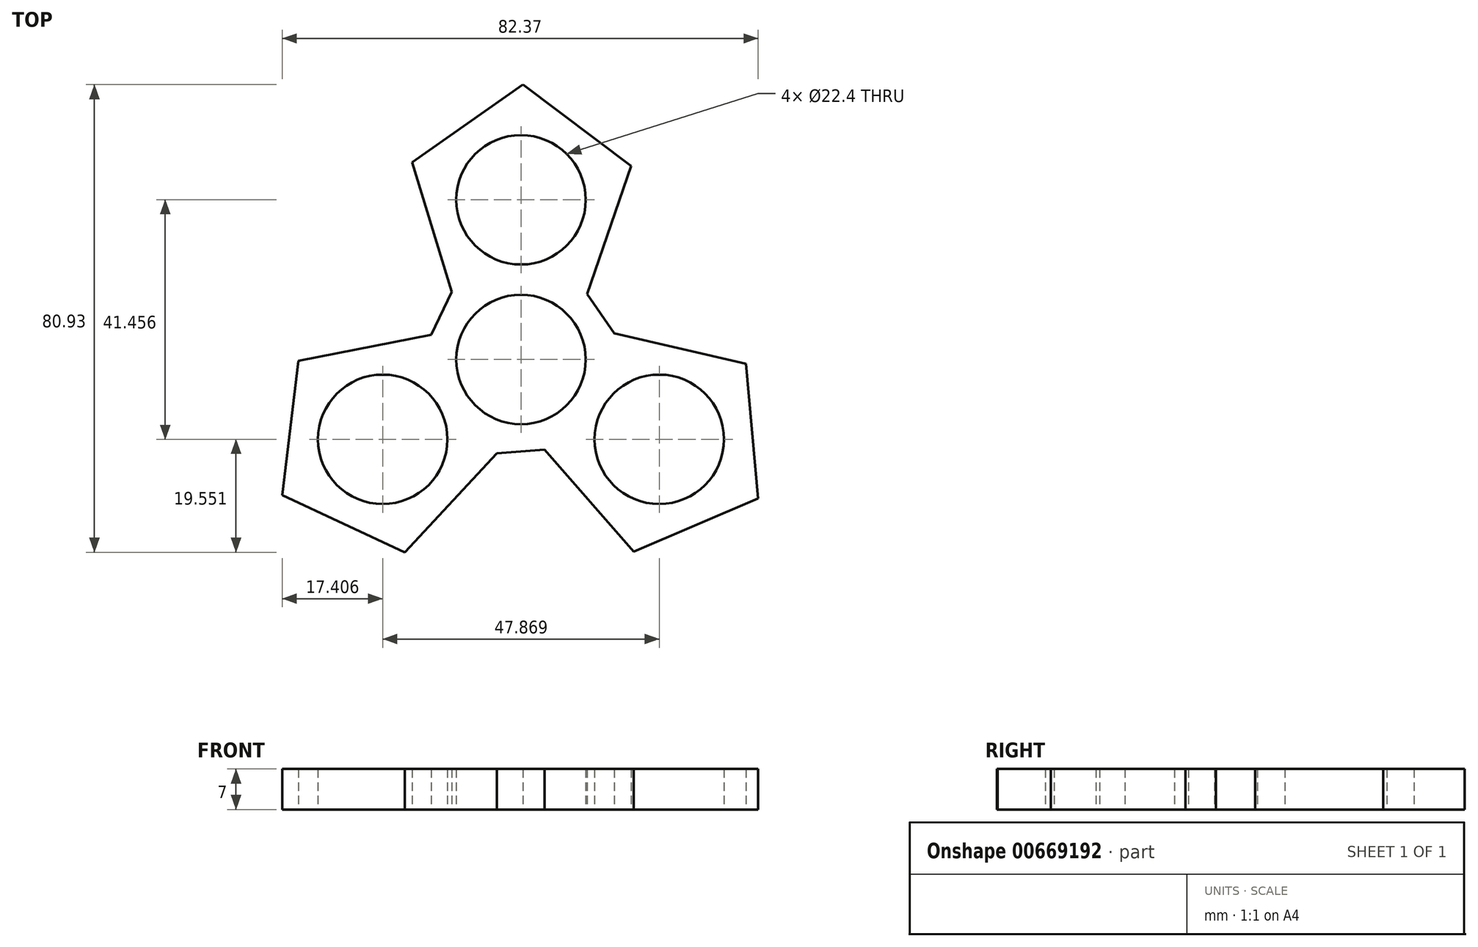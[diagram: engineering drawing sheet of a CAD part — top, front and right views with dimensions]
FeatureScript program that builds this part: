
annotation { "Feature Type Name" : "Feature", "Feature Type Description" : "" }
export const myFeature = defineFeature(function(context is Context, id is Id, definition is map)
    precondition{}
    {
        {
            var Q0;
            Q0=qCreatedBy(makeId("Top.planeOp"),FACE);
            var sketch = newSketch(context, id + "F0", { "sketchPlane" : qUnion([Q0])});
            skCircle(sketch, "E0", {"center": v(0, 0) * mm, "radius": 11.2 * mm});
            skCircle(sketch, "E1", {"center": v(0, 27.64) * mm, "radius": 11.2 * mm});
            skLineSegment(sketch, "E2.0", {"start": v(0.32, 47.56) * mm, "end": v(19.04, 33.5) * mm});
            skLineSegment(sketch, "E2.1", {"start": v(19.04, 33.5) * mm, "end": v(11.45, 11.34) * mm});
            skLineSegment(sketch, "E2.3", {"start": v(-11.96, 11.7) * mm, "end": v(-18.85, 34.1) * mm});
            skLineSegment(sketch, "E2.4", {"start": v(-18.85, 34.1) * mm, "end": v(0.32, 47.56) * mm});
            skPoint(sketch, "E2.0.midPoint", {"position": v(9.68, 40.52) * mm});
            skCircle(sketch, "E3.1.0", {"center": v(-23.93, -13.82) * mm, "radius": 11.2 * mm});
            skLineSegment(sketch, "E3.1.2", {"start": v(-41.34, -23.5) * mm, "end": v(-38.53, -0.25) * mm});
            skLineSegment(sketch, "E3.1.3", {"start": v(-20.1, -33.37) * mm, "end": v(-41.34, -23.5) * mm});
            skLineSegment(sketch, "E3.1.4", {"start": v(-4.16, -16.22) * mm, "end": v(-20.1, -33.37) * mm});
            skLineSegment(sketch, "E3.1.6", {"start": v(-38.53, -0.25) * mm, "end": v(-15.54, 4.25) * mm});
            skCircle(sketch, "E3.2.0", {"center": v(23.93, -13.82) * mm, "radius": 11.2 * mm});
            skLineSegment(sketch, "E3.2.2", {"start": v(41.03, -24.05) * mm, "end": v(19.48, -33.24) * mm});
            skLineSegment(sketch, "E3.2.3", {"start": v(38.95, -0.73) * mm, "end": v(41.03, -24.05) * mm});
            skLineSegment(sketch, "E3.2.4", {"start": v(16.12, 4.5) * mm, "end": v(38.95, -0.73) * mm});
            skLineSegment(sketch, "E3.2.6", {"start": v(19.48, -33.24) * mm, "end": v(4.1, -15.59) * mm});
            skLineSegment(sketch, "E4", {"start": v(-15.54, 4.25) * mm, "end": v(-11.96, 11.7) * mm});
            skLineSegment(sketch, "E5", {"start": v(11.45, 11.34) * mm, "end": v(16.12, 4.5) * mm});
            skLineSegment(sketch, "E6", {"start": v(-4.16, -16.22) * mm, "end": v(4.1, -15.59) * mm});
            skSolve(sketch);
        }
        {
            var Q0;
            Q0=makeQuery(id+"F0.imprint","IMPRINT",FACE,{"disambiguationData":[TD([[makeQuery(id+"F0.imprint","IMPRINT",EDGE,{"derivedFrom":sQuery(id+"F0.wireOp",EDGE,"E0")}),-1.0]])]});
            extrude(context, id + "F1", {"entities" : qUnion([Q0]), "depth" : 7 * mm, "offsetDistance" : 25 * mm});
        }
    });
